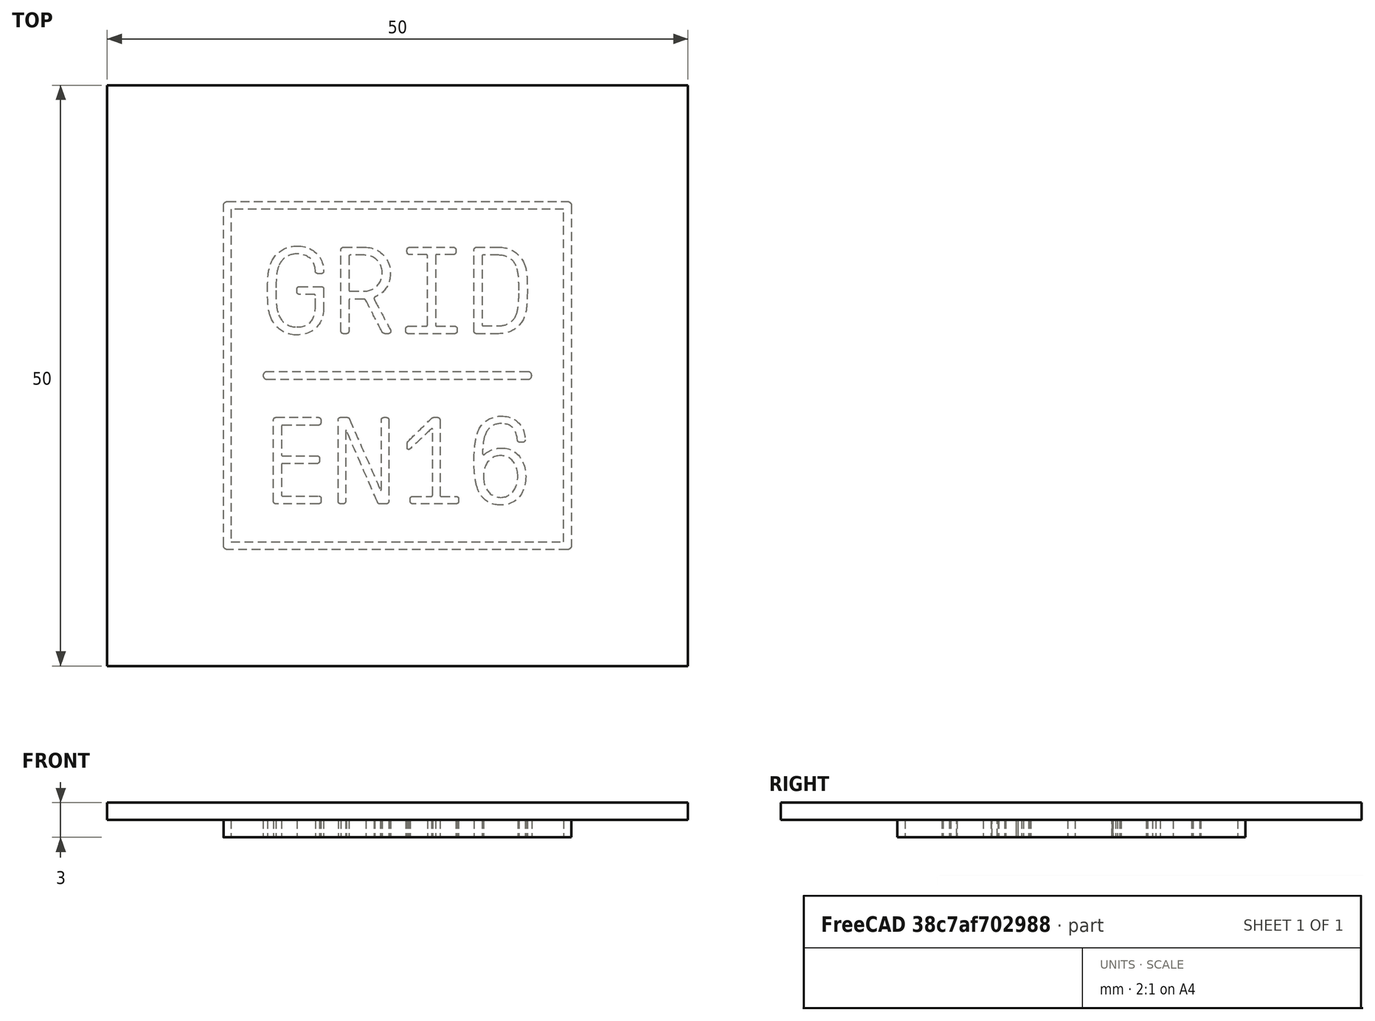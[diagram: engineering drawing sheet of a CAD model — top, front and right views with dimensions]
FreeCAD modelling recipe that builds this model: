
FCSTD DOCUMENT  (FreeCAD 0.18R16131 (Git))
Label: En16 Logo 5cm
License: All rights reserved
LicenseURL: http://en.wikipedia.org/wiki/All_rights_reserved
objects: Sketcher::SketchObject×3, PartDesign::Pad×3, PartDesign::Body×1
note: 10 computed .brp shape members not serialized (recipe doc carries the construction recipe); baked Part::Feature solids carry a one-line shape summary decoded from their .brp

FEATURE [Sketcher::SketchObject] Sketch014
  sketch-geometry (12):
    g0: BSplineCurve PolesCount=2 KnotsCount=2 Degree=1 IsPeriodic=0
    g1: BSplineCurve PolesCount=2 KnotsCount=2 Degree=1 IsPeriodic=0
    g2: BSplineCurve PolesCount=2 KnotsCount=2 Degree=1 IsPeriodic=0
    g3: BSplineCurve PolesCount=2 KnotsCount=2 Degree=1 IsPeriodic=0
    g4: BSplineCurve PolesCount=2 KnotsCount=2 Degree=1 IsPeriodic=0
    g5: BSplineCurve PolesCount=4 KnotsCount=2 Degree=3 IsPeriodic=0
    g6: BSplineCurve PolesCount=2 KnotsCount=2 Degree=1 IsPeriodic=0
    g7: BSplineCurve PolesCount=4 KnotsCount=2 Degree=3 IsPeriodic=0
    g8: BSplineCurve PolesCount=2 KnotsCount=2 Degree=1 IsPeriodic=0
    g9: BSplineCurve PolesCount=4 KnotsCount=2 Degree=3 IsPeriodic=0
    g10: BSplineCurve PolesCount=2 KnotsCount=2 Degree=1 IsPeriodic=0
    g11: BSplineCurve PolesCount=4 KnotsCount=2 Degree=3 IsPeriodic=0
  constraints (12):
    c: Coincident(g0,g1)
    c: Coincident(g1,g2)
    c: Coincident(g2,g3)
    c: Coincident(g3,g0)
    c: Coincident(g4,g5)
    c: Coincident(g5,g6)
    c: Coincident(g6,g7)
    c: Coincident(g7,g8)
    c: Coincident(g8,g9)
    c: Coincident(g9,g10)
    c: Coincident(g10,g11)
    c: Coincident(g11,g4)
FEATURE [Sketcher::SketchObject] Sketch015
  sketch-geometry (184):
    g0: BSplineCurve PolesCount=2 KnotsCount=2 Degree=1 IsPeriodic=0
    g1: BSplineCurve PolesCount=4 KnotsCount=2 Degree=3 IsPeriodic=0
    g2: BSplineCurve PolesCount=2 KnotsCount=2 Degree=1 IsPeriodic=0
    g3: BSplineCurve PolesCount=4 KnotsCount=2 Degree=3 IsPeriodic=0
    g4: BSplineCurve PolesCount=4 KnotsCount=2 Degree=3 IsPeriodic=0
    g5: BSplineCurve PolesCount=4 KnotsCount=2 Degree=3 IsPeriodic=0
    g6: BSplineCurve PolesCount=4 KnotsCount=2 Degree=3 IsPeriodic=0
    g7: BSplineCurve PolesCount=2 KnotsCount=2 Degree=1 IsPeriodic=0
    g8: BSplineCurve PolesCount=4 KnotsCount=2 Degree=3 IsPeriodic=0
    g9: BSplineCurve PolesCount=4 KnotsCount=2 Degree=3 IsPeriodic=0
    g10: BSplineCurve PolesCount=2 KnotsCount=2 Degree=1 IsPeriodic=0
    g11: BSplineCurve PolesCount=4 KnotsCount=2 Degree=3 IsPeriodic=0
    g12: BSplineCurve PolesCount=2 KnotsCount=2 Degree=1 IsPeriodic=0
    g13: BSplineCurve PolesCount=4 KnotsCount=2 Degree=3 IsPeriodic=0
    g14: BSplineCurve PolesCount=2 KnotsCount=2 Degree=1 IsPeriodic=0
    g15: BSplineCurve PolesCount=4 KnotsCount=2 Degree=3 IsPeriodic=0
    g16: BSplineCurve PolesCount=2 KnotsCount=2 Degree=1 IsPeriodic=0
    g17: BSplineCurve PolesCount=4 KnotsCount=2 Degree=3 IsPeriodic=0
    g18: BSplineCurve PolesCount=2 KnotsCount=2 Degree=1 IsPeriodic=0
    g19: BSplineCurve PolesCount=4 KnotsCount=2 Degree=3 IsPeriodic=0
    g20: BSplineCurve PolesCount=4 KnotsCount=2 Degree=3 IsPeriodic=0
    g21: BSplineCurve PolesCount=2 KnotsCount=2 Degree=1 IsPeriodic=0
    g22: BSplineCurve PolesCount=4 KnotsCount=2 Degree=3 IsPeriodic=0
    g23: BSplineCurve PolesCount=4 KnotsCount=2 Degree=3 IsPeriodic=0
    g24: BSplineCurve PolesCount=2 KnotsCount=2 Degree=1 IsPeriodic=0
    g25: BSplineCurve PolesCount=4 KnotsCount=2 Degree=3 IsPeriodic=0
    g26: BSplineCurve PolesCount=4 KnotsCount=2 Degree=3 IsPeriodic=0
    g27: BSplineCurve PolesCount=2 KnotsCount=2 Degree=1 IsPeriodic=0
    g28: BSplineCurve PolesCount=4 KnotsCount=2 Degree=3 IsPeriodic=0
    g29: BSplineCurve PolesCount=2 KnotsCount=2 Degree=1 IsPeriodic=0
    g30: BSplineCurve PolesCount=4 KnotsCount=2 Degree=3 IsPeriodic=0
    g31: BSplineCurve PolesCount=2 KnotsCount=2 Degree=1 IsPeriodic=0
    g32: BSplineCurve PolesCount=4 KnotsCount=2 Degree=3 IsPeriodic=0
    g33: BSplineCurve PolesCount=4 KnotsCount=2 Degree=3 IsPeriodic=0
    g34: BSplineCurve PolesCount=4 KnotsCount=2 Degree=3 IsPeriodic=0
    g35: BSplineCurve PolesCount=4 KnotsCount=2 Degree=3 IsPeriodic=0
    g36: BSplineCurve PolesCount=4 KnotsCount=2 Degree=3 IsPeriodic=0
    g37: BSplineCurve PolesCount=4 KnotsCount=2 Degree=3 IsPeriodic=0
    g38: BSplineCurve PolesCount=2 KnotsCount=2 Degree=1 IsPeriodic=0
    g39: BSplineCurve PolesCount=4 KnotsCount=2 Degree=3 IsPeriodic=0
    g40: BSplineCurve PolesCount=4 KnotsCount=2 Degree=3 IsPeriodic=0
    g41: BSplineCurve PolesCount=4 KnotsCount=2 Degree=3 IsPeriodic=0
    g42: BSplineCurve PolesCount=4 KnotsCount=2 Degree=3 IsPeriodic=0
    g43: BSplineCurve PolesCount=4 KnotsCount=2 Degree=3 IsPeriodic=0
    g44: BSplineCurve PolesCount=4 KnotsCount=2 Degree=3 IsPeriodic=0
    g45: BSplineCurve PolesCount=4 KnotsCount=2 Degree=3 IsPeriodic=0
    g46: BSplineCurve PolesCount=2 KnotsCount=2 Degree=1 IsPeriodic=0
    g47: BSplineCurve PolesCount=4 KnotsCount=2 Degree=3 IsPeriodic=0
    g48: BSplineCurve PolesCount=2 KnotsCount=2 Degree=1 IsPeriodic=0
    g49: BSplineCurve PolesCount=4 KnotsCount=2 Degree=3 IsPeriodic=0
    g50: BSplineCurve PolesCount=2 KnotsCount=2 Degree=1 IsPeriodic=0
    g51: BSplineCurve PolesCount=4 KnotsCount=2 Degree=3 IsPeriodic=0
    g52: BSplineCurve PolesCount=2 KnotsCount=2 Degree=1 IsPeriodic=0
    g53: BSplineCurve PolesCount=4 KnotsCount=2 Degree=3 IsPeriodic=0
    g54: BSplineCurve PolesCount=2 KnotsCount=2 Degree=1 IsPeriodic=0
    g55: BSplineCurve PolesCount=4 KnotsCount=2 Degree=3 IsPeriodic=0
    g56: BSplineCurve PolesCount=4 KnotsCount=2 Degree=3 IsPeriodic=0
    g57: BSplineCurve PolesCount=2 KnotsCount=2 Degree=1 IsPeriodic=0
    g58: BSplineCurve PolesCount=4 KnotsCount=2 Degree=3 IsPeriodic=0
    g59: BSplineCurve PolesCount=2 KnotsCount=2 Degree=1 IsPeriodic=0
    g60: BSplineCurve PolesCount=4 KnotsCount=2 Degree=3 IsPeriodic=0
    g61: BSplineCurve PolesCount=2 KnotsCount=2 Degree=1 IsPeriodic=0
    g62: BSplineCurve PolesCount=4 KnotsCount=2 Degree=3 IsPeriodic=0
    g63: BSplineCurve PolesCount=2 KnotsCount=2 Degree=1 IsPeriodic=0
    g64: BSplineCurve PolesCount=4 KnotsCount=2 Degree=3 IsPeriodic=0
    g65: BSplineCurve PolesCount=2 KnotsCount=2 Degree=1 IsPeriodic=0
    g66: BSplineCurve PolesCount=4 KnotsCount=2 Degree=3 IsPeriodic=0
    g67: BSplineCurve PolesCount=2 KnotsCount=2 Degree=1 IsPeriodic=0
    g68: BSplineCurve PolesCount=4 KnotsCount=2 Degree=3 IsPeriodic=0
    g69: BSplineCurve PolesCount=2 KnotsCount=2 Degree=1 IsPeriodic=0
    g70: BSplineCurve PolesCount=4 KnotsCount=2 Degree=3 IsPeriodic=0
    g71: BSplineCurve PolesCount=2 KnotsCount=2 Degree=1 IsPeriodic=0
    g72: BSplineCurve PolesCount=4 KnotsCount=2 Degree=3 IsPeriodic=0
    g73: BSplineCurve PolesCount=2 KnotsCount=2 Degree=1 IsPeriodic=0
    g74: BSplineCurve PolesCount=4 KnotsCount=2 Degree=3 IsPeriodic=0
    g75: BSplineCurve PolesCount=2 KnotsCount=2 Degree=1 IsPeriodic=0
    g76: BSplineCurve PolesCount=4 KnotsCount=2 Degree=3 IsPeriodic=0
    g77: BSplineCurve PolesCount=2 KnotsCount=2 Degree=1 IsPeriodic=0
    g78: BSplineCurve PolesCount=4 KnotsCount=2 Degree=3 IsPeriodic=0
    g79: BSplineCurve PolesCount=2 KnotsCount=2 Degree=1 IsPeriodic=0
    g80: BSplineCurve PolesCount=4 KnotsCount=2 Degree=3 IsPeriodic=0
    g81: BSplineCurve PolesCount=2 KnotsCount=2 Degree=1 IsPeriodic=0
    g82: BSplineCurve PolesCount=4 KnotsCount=2 Degree=3 IsPeriodic=0
    g83: BSplineCurve PolesCount=2 KnotsCount=2 Degree=1 IsPeriodic=0
    g84: BSplineCurve PolesCount=4 KnotsCount=2 Degree=3 IsPeriodic=0
    g85: BSplineCurve PolesCount=2 KnotsCount=2 Degree=1 IsPeriodic=0
    g86: BSplineCurve PolesCount=4 KnotsCount=2 Degree=3 IsPeriodic=0
    g87: BSplineCurve PolesCount=2 KnotsCount=2 Degree=1 IsPeriodic=0
    g88: BSplineCurve PolesCount=4 KnotsCount=2 Degree=3 IsPeriodic=0
    g89: BSplineCurve PolesCount=2 KnotsCount=2 Degree=1 IsPeriodic=0
    g90: BSplineCurve PolesCount=4 KnotsCount=2 Degree=3 IsPeriodic=0
    g91: BSplineCurve PolesCount=2 KnotsCount=2 Degree=1 IsPeriodic=0
    g92: BSplineCurve PolesCount=4 KnotsCount=2 Degree=3 IsPeriodic=0
    g93: BSplineCurve PolesCount=2 KnotsCount=2 Degree=1 IsPeriodic=0
    g94: BSplineCurve PolesCount=4 KnotsCount=2 Degree=3 IsPeriodic=0
    g95: BSplineCurve PolesCount=2 KnotsCount=2 Degree=1 IsPeriodic=0
    g96: BSplineCurve PolesCount=4 KnotsCount=2 Degree=3 IsPeriodic=0
    g97: BSplineCurve PolesCount=2 KnotsCount=2 Degree=1 IsPeriodic=0
    g98: BSplineCurve PolesCount=4 KnotsCount=2 Degree=3 IsPeriodic=0
    g99: BSplineCurve PolesCount=4 KnotsCount=2 Degree=3 IsPeriodic=0
    g100: BSplineCurve PolesCount=4 KnotsCount=2 Degree=3 IsPeriodic=0
    g101: BSplineCurve PolesCount=4 KnotsCount=2 Degree=3 IsPeriodic=0
    g102: BSplineCurve PolesCount=2 KnotsCount=2 Degree=1 IsPeriodic=0
    g103: BSplineCurve PolesCount=4 KnotsCount=2 Degree=3 IsPeriodic=0
    g104: BSplineCurve PolesCount=2 KnotsCount=2 Degree=1 IsPeriodic=0
    g105: BSplineCurve PolesCount=4 KnotsCount=2 Degree=3 IsPeriodic=0
    g106: BSplineCurve PolesCount=2 KnotsCount=2 Degree=1 IsPeriodic=0
    g107: BSplineCurve PolesCount=4 KnotsCount=2 Degree=3 IsPeriodic=0
    g108: BSplineCurve PolesCount=4 KnotsCount=2 Degree=3 IsPeriodic=0
    g109: BSplineCurve PolesCount=4 KnotsCount=2 Degree=3 IsPeriodic=0
    g110: BSplineCurve PolesCount=4 KnotsCount=2 Degree=3 IsPeriodic=0
    g111: BSplineCurve PolesCount=4 KnotsCount=2 Degree=3 IsPeriodic=0
    g112: BSplineCurve PolesCount=2 KnotsCount=2 Degree=1 IsPeriodic=0
    g113: BSplineCurve PolesCount=4 KnotsCount=2 Degree=3 IsPeriodic=0
    g114: BSplineCurve PolesCount=2 KnotsCount=2 Degree=1 IsPeriodic=0
    g115: BSplineCurve PolesCount=4 KnotsCount=2 Degree=3 IsPeriodic=0
    g116: BSplineCurve PolesCount=4 KnotsCount=2 Degree=3 IsPeriodic=0
    g117: BSplineCurve PolesCount=4 KnotsCount=2 Degree=3 IsPeriodic=0
    g118: BSplineCurve PolesCount=4 KnotsCount=2 Degree=3 IsPeriodic=0
    g119: BSplineCurve PolesCount=2 KnotsCount=2 Degree=1 IsPeriodic=0
    g120: BSplineCurve PolesCount=4 KnotsCount=2 Degree=3 IsPeriodic=0
    g121: BSplineCurve PolesCount=2 KnotsCount=2 Degree=1 IsPeriodic=0
    g122: BSplineCurve PolesCount=4 KnotsCount=2 Degree=3 IsPeriodic=0
    g123: BSplineCurve PolesCount=2 KnotsCount=2 Degree=1 IsPeriodic=0
    g124: BSplineCurve PolesCount=4 KnotsCount=2 Degree=3 IsPeriodic=0
    g125: BSplineCurve PolesCount=2 KnotsCount=2 Degree=1 IsPeriodic=0
    g126: BSplineCurve PolesCount=4 KnotsCount=2 Degree=3 IsPeriodic=0
    g127: BSplineCurve PolesCount=2 KnotsCount=2 Degree=1 IsPeriodic=0
    g128: BSplineCurve PolesCount=4 KnotsCount=2 Degree=3 IsPeriodic=0
    g129: BSplineCurve PolesCount=2 KnotsCount=2 Degree=1 IsPeriodic=0
    g130: BSplineCurve PolesCount=4 KnotsCount=2 Degree=3 IsPeriodic=0
    g131: BSplineCurve PolesCount=2 KnotsCount=2 Degree=1 IsPeriodic=0
    g132: BSplineCurve PolesCount=4 KnotsCount=2 Degree=3 IsPeriodic=0
    g133: BSplineCurve PolesCount=2 KnotsCount=2 Degree=1 IsPeriodic=0
    g134: BSplineCurve PolesCount=4 KnotsCount=2 Degree=3 IsPeriodic=0
    g135: BSplineCurve PolesCount=2 KnotsCount=2 Degree=1 IsPeriodic=0
    g136: BSplineCurve PolesCount=4 KnotsCount=2 Degree=3 IsPeriodic=0
    g137: BSplineCurve PolesCount=2 KnotsCount=2 Degree=1 IsPeriodic=0
    g138: BSplineCurve PolesCount=4 KnotsCount=2 Degree=3 IsPeriodic=0
    g139: BSplineCurve PolesCount=2 KnotsCount=2 Degree=1 IsPeriodic=0
    g140: BSplineCurve PolesCount=4 KnotsCount=2 Degree=3 IsPeriodic=0
    g141: BSplineCurve PolesCount=2 KnotsCount=2 Degree=1 IsPeriodic=0
    g142: BSplineCurve PolesCount=4 KnotsCount=2 Degree=3 IsPeriodic=0
    g143: BSplineCurve PolesCount=2 KnotsCount=2 Degree=1 IsPeriodic=0
    g144: BSplineCurve PolesCount=4 KnotsCount=2 Degree=3 IsPeriodic=0
    g145: BSplineCurve PolesCount=4 KnotsCount=2 Degree=3 IsPeriodic=0
    g146: BSplineCurve PolesCount=4 KnotsCount=2 Degree=3 IsPeriodic=0
    g147: BSplineCurve PolesCount=4 KnotsCount=2 Degree=3 IsPeriodic=0
    g148: BSplineCurve PolesCount=4 KnotsCount=2 Degree=3 IsPeriodic=0
    g149: BSplineCurve PolesCount=4 KnotsCount=2 Degree=3 IsPeriodic=0
    g150: BSplineCurve PolesCount=2 KnotsCount=2 Degree=1 IsPeriodic=0
    g151: BSplineCurve PolesCount=4 KnotsCount=2 Degree=3 IsPeriodic=0
    g152: BSplineCurve PolesCount=4 KnotsCount=2 Degree=3 IsPeriodic=0
    g153: BSplineCurve PolesCount=4 KnotsCount=2 Degree=3 IsPeriodic=0
    g154: BSplineCurve PolesCount=4 KnotsCount=2 Degree=3 IsPeriodic=0
    g155: BSplineCurve PolesCount=4 KnotsCount=2 Degree=3 IsPeriodic=0
    g156: BSplineCurve PolesCount=4 KnotsCount=2 Degree=3 IsPeriodic=0
    g157: BSplineCurve PolesCount=4 KnotsCount=2 Degree=3 IsPeriodic=0
    g158: BSplineCurve PolesCount=4 KnotsCount=2 Degree=3 IsPeriodic=0
    g159: BSplineCurve PolesCount=4 KnotsCount=2 Degree=3 IsPeriodic=0
    g160: BSplineCurve PolesCount=2 KnotsCount=2 Degree=1 IsPeriodic=0
    g161: BSplineCurve PolesCount=4 KnotsCount=2 Degree=3 IsPeriodic=0
    g162: BSplineCurve PolesCount=2 KnotsCount=2 Degree=1 IsPeriodic=0
    g163: BSplineCurve PolesCount=4 KnotsCount=2 Degree=3 IsPeriodic=0
    g164: BSplineCurve PolesCount=2 KnotsCount=2 Degree=1 IsPeriodic=0
    g165: BSplineCurve PolesCount=4 KnotsCount=2 Degree=3 IsPeriodic=0
    g166: BSplineCurve PolesCount=2 KnotsCount=2 Degree=1 IsPeriodic=0
    g167: BSplineCurve PolesCount=4 KnotsCount=2 Degree=3 IsPeriodic=0
    g168: BSplineCurve PolesCount=2 KnotsCount=2 Degree=1 IsPeriodic=0
    g169: BSplineCurve PolesCount=4 KnotsCount=2 Degree=3 IsPeriodic=0
    g170: BSplineCurve PolesCount=2 KnotsCount=2 Degree=1 IsPeriodic=0
    g171: BSplineCurve PolesCount=4 KnotsCount=2 Degree=3 IsPeriodic=0
    g172: BSplineCurve PolesCount=2 KnotsCount=2 Degree=1 IsPeriodic=0
    g173: BSplineCurve PolesCount=4 KnotsCount=2 Degree=3 IsPeriodic=0
    g174: BSplineCurve PolesCount=2 KnotsCount=2 Degree=1 IsPeriodic=0
    g175: BSplineCurve PolesCount=4 KnotsCount=2 Degree=3 IsPeriodic=0
    g176: BSplineCurve PolesCount=2 KnotsCount=2 Degree=1 IsPeriodic=0
    g177: BSplineCurve PolesCount=4 KnotsCount=2 Degree=3 IsPeriodic=0
    g178: BSplineCurve PolesCount=2 KnotsCount=2 Degree=1 IsPeriodic=0
    g179: BSplineCurve PolesCount=4 KnotsCount=2 Degree=3 IsPeriodic=0
    g180: BSplineCurve PolesCount=2 KnotsCount=2 Degree=1 IsPeriodic=0
    g181: BSplineCurve PolesCount=4 KnotsCount=2 Degree=3 IsPeriodic=0
    g182: BSplineCurve PolesCount=2 KnotsCount=2 Degree=1 IsPeriodic=0
    g183: BSplineCurve PolesCount=4 KnotsCount=2 Degree=3 IsPeriodic=0
  constraints (184):
    c: Coincident(g0,g1)
    c: Coincident(g1,g2)
    c: Coincident(g2,g3)
    c: Coincident(g3,g4)
    c: Coincident(g4,g5)
    c: Coincident(g5,g6)
    c: Coincident(g6,g7)
    c: Coincident(g7,g8)
    c: Coincident(g8,g9)
    c: Coincident(g9,g10)
    c: Coincident(g10,g11)
    c: Coincident(g11,g12)
    c: Coincident(g12,g13)
    c: Coincident(g13,g14)
    c: Coincident(g14,g15)
    c: Coincident(g15,g16)
    c: Coincident(g16,g17)
    c: Coincident(g17,g18)
    c: Coincident(g18,g19)
    c: Coincident(g19,g0)
    c: Coincident(g20,g21)
    c: Coincident(g21,g22)
    c: Coincident(g22,g23)
    c: Coincident(g23,g24)
    c: Coincident(g24,g25)
    c: Coincident(g25,g20)
    c: Coincident(g26,g27)
    c: Coincident(g27,g28)
    c: Coincident(g28,g29)
    c: Coincident(g29,g30)
    c: Coincident(g30,g31)
    c: Coincident(g31,g32)
    c: Coincident(g32,g26)
    c: Coincident(g33,g34)
    c: Coincident(g34,g35)
    c: Coincident(g35,g36)
    c: Coincident(g36,g37)
    c: Coincident(g37,g38)
    c: Coincident(g38,g39)
    c: Coincident(g39,g40)
    c: Coincident(g40,g41)
    c: Coincident(g41,g42)
    c: Coincident(g42,g43)
    c: Coincident(g43,g44)
    c: Coincident(g44,g45)
    c: Coincident(g45,g46)
    c: Coincident(g46,g47)
    c: Coincident(g47,g48)
    c: Coincident(g48,g49)
    c: Coincident(g49,g50)
    c: Coincident(g50,g51)
    c: Coincident(g51,g52)
    c: Coincident(g52,g53)
    c: Coincident(g53,g54)
    c: Coincident(g54,g55)
    c: Coincident(g55,g56)
    c: Coincident(g56,g33)
    c: Coincident(g57,g58)
    c: Coincident(g58,g59)
    c: Coincident(g59,g60)
    c: Coincident(g60,g61)
    c: Coincident(g61,g62)
    c: Coincident(g62,g63)
    c: Coincident(g63,g64)
    c: Coincident(g64,g65)
    c: Coincident(g65,g66)
    c: Coincident(g66,g67)
    c: Coincident(g67,g68)
    c: Coincident(g68,g69)
    c: Coincident(g69,g70)
    c: Coincident(g70,g71)
    c: Coincident(g71,g72)
    c: Coincident(g72,g73)
    c: Coincident(g73,g74)
    c: Coincident(g74,g75)
    c: Coincident(g75,g76)
    c: Coincident(g76,g77)
    c: Coincident(g77,g78)
    c: Coincident(g78,g57)
    c: Coincident(g79,g80)
    c: Coincident(g80,g81)
    c: Coincident(g81,g82)
    c: Coincident(g82,g83)
    c: Coincident(g83,g84)
    c: Coincident(g84,g85)
    c: Coincident(g85,g86)
    c: Coincident(g86,g87)
    c: Coincident(g87,g88)
    c: Coincident(g88,g89)
    c: Coincident(g89,g90)
    c: Coincident(g90,g91)
    c: Coincident(g91,g92)
    c: Coincident(g92,g93)
    c: Coincident(g93,g94)
    c: Coincident(g94,g95)
    c: Coincident(g95,g96)
    c: Coincident(g96,g97)
    c: Coincident(g97,g98)
    c: Coincident(g98,g79)
    c: Coincident(g99,g100)
    c: Coincident(g100,g101)
    c: Coincident(g101,g102)
    c: Coincident(g102,g103)
    c: Coincident(g103,g104)
    c: Coincident(g104,g105)
    c: Coincident(g105,g106)
    c: Coincident(g106,g107)
    c: Coincident(g107,g99)
    c: Coincident(g108,g109)
    c: Coincident(g109,g110)
    c: Coincident(g110,g111)
    c: Coincident(g111,g108)
    c: Coincident(g112,g113)
    c: Coincident(g113,g114)
    c: Coincident(g114,g115)
    c: Coincident(g115,g116)
    c: Coincident(g116,g117)
    c: Coincident(g117,g118)
    c: Coincident(g118,g119)
    c: Coincident(g119,g120)
    c: Coincident(g120,g112)
    c: Coincident(g121,g122)
    c: Coincident(g122,g123)
    c: Coincident(g123,g124)
    c: Coincident(g124,g125)
    c: Coincident(g125,g126)
    c: Coincident(g126,g127)
    c: Coincident(g127,g128)
    c: Coincident(g128,g129)
    c: Coincident(g129,g130)
    c: Coincident(g130,g131)
    c: Coincident(g131,g132)
    c: Coincident(g132,g133)
    c: Coincident(g133,g134)
    c: Coincident(g134,g135)
    c: Coincident(g135,g136)
    c: Coincident(g136,g137)
    c: Coincident(g137,g138)
    c: Coincident(g138,g139)
    c: Coincident(g139,g140)
    c: Coincident(g140,g141)
    c: Coincident(g141,g142)
    c: Coincident(g142,g143)
    c: Coincident(g143,g144)
    c: Coincident(g144,g121)
    c: Coincident(g145,g146)
    c: Coincident(g146,g147)
    c: Coincident(g147,g148)
    c: Coincident(g148,g149)
    c: Coincident(g149,g150)
    c: Coincident(g150,g151)
    c: Coincident(g151,g152)
    c: Coincident(g152,g153)
    c: Coincident(g153,g154)
    c: Coincident(g154,g155)
    c: Coincident(g155,g156)
    c: Coincident(g156,g157)
    c: Coincident(g157,g158)
    c: Coincident(g158,g159)
    c: Coincident(g159,g145)
    c: Coincident(g160,g161)
    c: Coincident(g161,g162)
    c: Coincident(g162,g163)
    c: Coincident(g163,g164)
    c: Coincident(g164,g165)
    c: Coincident(g165,g166)
    c: Coincident(g166,g167)
    c: Coincident(g167,g168)
    c: Coincident(g168,g169)
    c: Coincident(g169,g170)
    c: Coincident(g170,g171)
    c: Coincident(g171,g172)
    c: Coincident(g172,g173)
    c: Coincident(g173,g174)
    c: Coincident(g174,g175)
    c: Coincident(g175,g176)
    c: Coincident(g176,g177)
    c: Coincident(g177,g178)
    c: Coincident(g178,g179)
    c: Coincident(g179,g180)
    c: Coincident(g180,g181)
    c: Coincident(g181,g182)
    c: Coincident(g182,g183)
    c: Coincident(g183,g160)
FEATURE [Sketcher::SketchObject] Sketch
  MapMode = 5
  Support = -> [XY_Plane]
  sketch-geometry (5):
    g0: LineSegment StartX=-25 StartY=25 StartZ=0 EndX=-25 EndY=-25 EndZ=0
    g1: LineSegment StartX=-25 StartY=-25 StartZ=0 EndX=25 EndY=-25 EndZ=0
    g2: LineSegment StartX=25 StartY=-25 StartZ=0 EndX=25 EndY=25 EndZ=0
    g3: LineSegment StartX=25 StartY=25 StartZ=0 EndX=-25 EndY=25 EndZ=0
    g4: Circle [constr] CenterX=0 CenterY=0 CenterZ=0 NormalX=0 NormalY=0 NormalZ=1 AngleXU=0 Radius=35.3553
  constraints (14):
    c: Coincident(g0,g1)
    c: Coincident(g1,g2)
    c: Coincident(g2,g3)
    c: Coincident(g3,g0)
    c: Equal(g0,g1)
    c: Equal(g0,g2)
    c: Equal(g0,g3)
    c: PointOnObject(g0,g4)
    c: PointOnObject(g1,g4)
    c: PointOnObject(g2,g4)
    c: PointOnObject(g3,g4)
    c: Coincident(g4,g-1)
    c: Horizontal(g3)
    c: DistanceX(g3,g3) = 50
FEATURE [PartDesign::Pad] Pad
  Length = 1.5
  Length2 = 100
  Profile = -> Sketch
  Type = 0
FEATURE [PartDesign::Pad] Pad001
  BaseFeature = -> Pad
  Length = 1.5
  Length2 = 100
  Profile = -> Sketch014
  Reversed = true
  Type = 0
FEATURE [PartDesign::Pad] Pad002
  BaseFeature = -> Pad001
  Length = 1.5
  Length2 = 100
  Profile = -> Sketch015
  Reversed = true
  Type = 0
FEATURE [PartDesign::Body] Body
  Group = -> [Sketch,Pad,Sketch014,Sketch015,Pad001,Pad002]
  Origin = -> Origin
  Tip = -> Pad002
